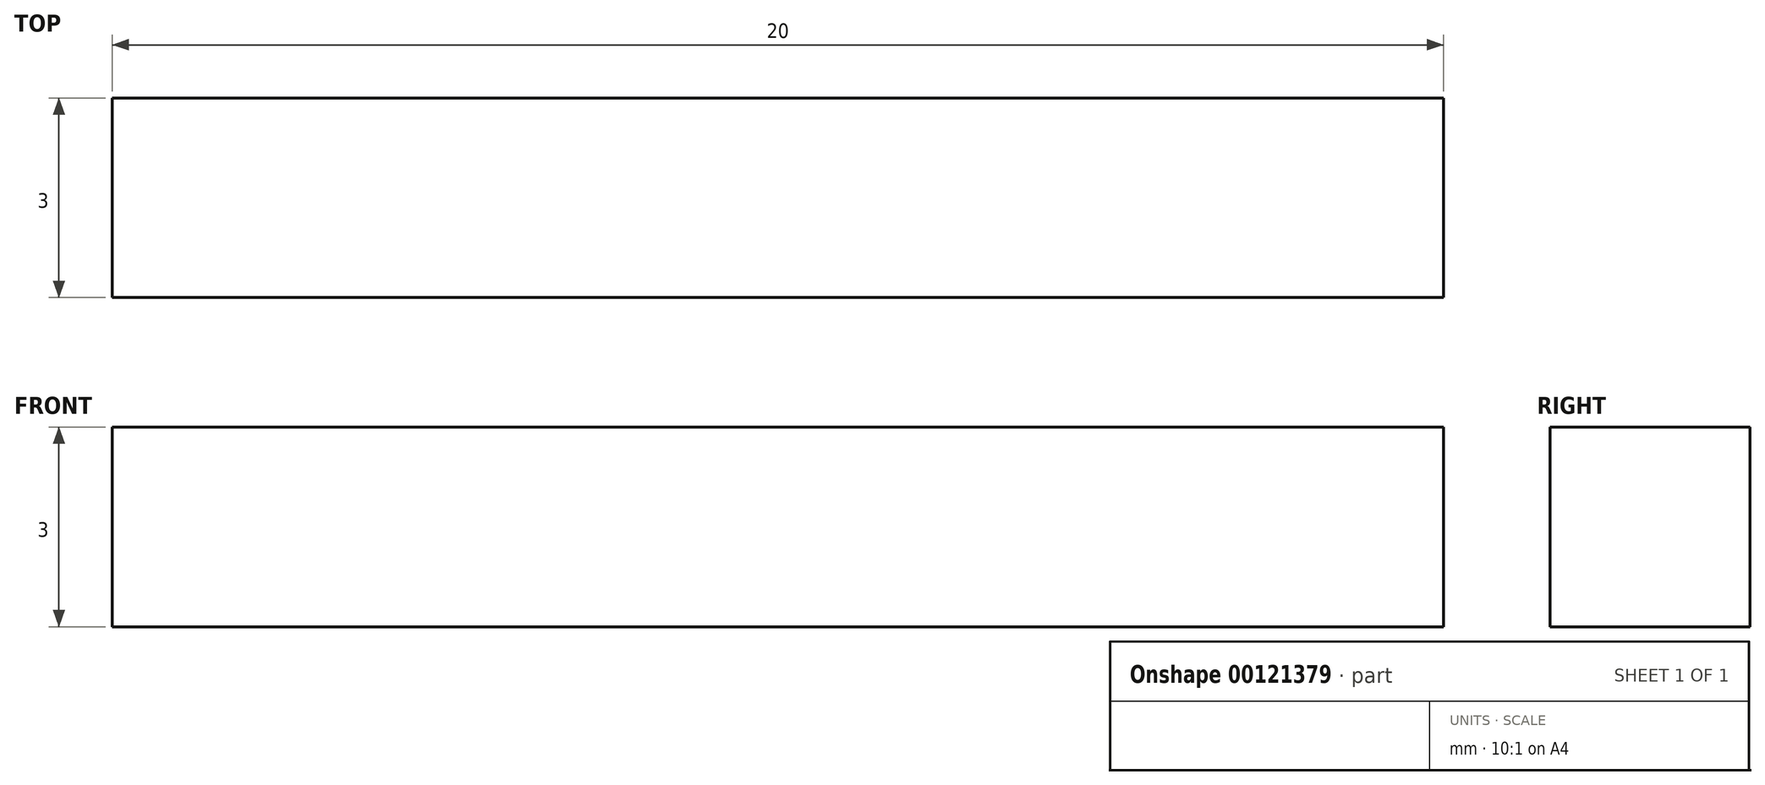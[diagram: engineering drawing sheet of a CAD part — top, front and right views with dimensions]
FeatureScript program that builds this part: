
annotation { "Feature Type Name" : "Feature", "Feature Type Description" : "" }
export const myFeature = defineFeature(function(context is Context, id is Id, definition is map)
    precondition{}
    {
        {
            var Q0;
            Q0=qCreatedBy(makeId("Front.planeOp"),FACE);
            var sketch = newSketch(context, id + "F0", { "sketchPlane" : qUnion([Q0])});
            skLineSegment(sketch, "E0.bottom", {"start": v(0, 3) * mm, "end": v(20, 3) * mm});
            skLineSegment(sketch, "E0.top", {"start": v(0, 0) * mm, "end": v(20, 0) * mm});
            skLineSegment(sketch, "E0.left", {"start": v(0, 3) * mm, "end": v(0, 0) * mm});
            skLineSegment(sketch, "E0.right", {"start": v(20, 3) * mm, "end": v(20, 0) * mm});
            skSolve(sketch);
        }
        {
            var Q0;
            Q0 = qSketchRegion(id + "F0", true);
            extrude(context, id + "F1", {"entities" : qUnion([Q0]), "depth" : 3 * mm});
        }
    });
